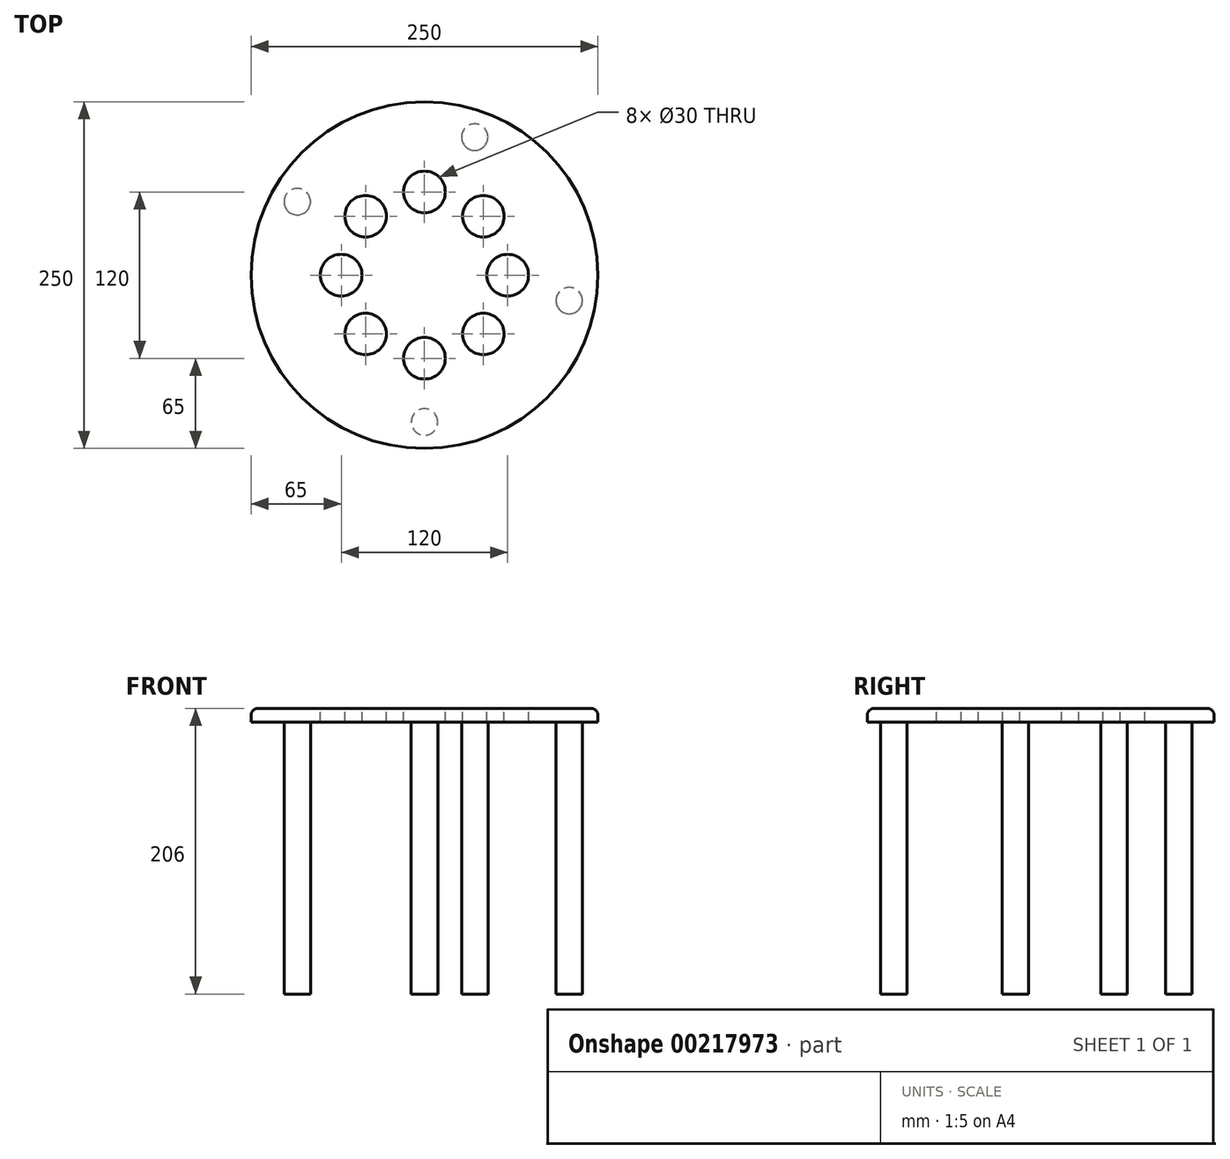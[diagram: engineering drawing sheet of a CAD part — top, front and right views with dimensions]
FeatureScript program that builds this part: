
annotation { "Feature Type Name" : "Feature", "Feature Type Description" : "" }
export const myFeature = defineFeature(function(context is Context, id is Id, definition is map)
    precondition{}
    {
        {
            var Q0;
            Q0=qCreatedBy(makeId("Top.planeOp"),FACE);
            var sketch = newSketch(context, id + "F0", { "sketchPlane" : qUnion([Q0])});
            skCircle(sketch, "E0", {"center": v(0, 0) * mm, "radius": 125 * mm});
            skSolve(sketch);
        }
        {
            var Q0;
            Q0=makeQuery(id+"F0.imprint","IMPRINT",FACE,{"disambiguationData":[TD([[makeQuery(id+"F0.imprint","IMPRINT",EDGE,{"derivedFrom":sQuery(id+"F0.wireOp",EDGE,"E0")}),1.0]])]});
            var sketch = newSketch(context, id + "F1", { "sketchPlane" : qUnion([Q0])});
            skCircle(sketch, "E1", {"center": v(0, 60) * mm, "radius": 15 * mm});
            skCircle(sketch, "E2.1.0", {"center": v(-42.43, 42.43) * mm, "radius": 15 * mm});
            skCircle(sketch, "E2.2.0", {"center": v(-60, 0) * mm, "radius": 15 * mm});
            skCircle(sketch, "E2.3.0", {"center": v(-42.43, -42.43) * mm, "radius": 15 * mm});
            skCircle(sketch, "E2.4.0", {"center": v(0, -60) * mm, "radius": 15 * mm});
            skCircle(sketch, "E2.5.0", {"center": v(42.43, -42.43) * mm, "radius": 15 * mm});
            skCircle(sketch, "E2.6.0", {"center": v(60, 0) * mm, "radius": 15 * mm});
            skCircle(sketch, "E2.7.0", {"center": v(42.43, 42.43) * mm, "radius": 15 * mm});
            skPoint(sketch, "E2.center", {"position": v(0, 0) * mm});
            skSolve(sketch);
        }
        {
            var Q0;
            Q0=makeQuery(id+"F0.imprint","IMPRINT",FACE,{"disambiguationData":[TD([[makeQuery(id+"F0.imprint","IMPRINT",EDGE,{"derivedFrom":sQuery(id+"F0.wireOp",EDGE,"E0")}),1.0]])]});
            extrude(context, id + "F2", {"entities" : qUnion([Q0]), "oppositeDirection" : true, "depth" : 10 * mm});
        }
        {
            var Q0;
            Q0=makeQuery(id+"F1.imprint","IMPRINT",FACE,{"disambiguationData":[TD([[makeQuery(id+"F1.imprint","IMPRINT",EDGE,{"derivedFrom":sQuery(id+"F1.wireOp",EDGE,"E2.1.0")}),1.0]])]});
            var Q1;
            Q1=makeQuery(id+"F1.imprint","IMPRINT",FACE,{"disambiguationData":[TD([[makeQuery(id+"F1.imprint","IMPRINT",EDGE,{"derivedFrom":sQuery(id+"F1.wireOp",EDGE,"E1")}),1.0]])]});
            var Q2;
            Q2=makeQuery(id+"F1.imprint","IMPRINT",FACE,{"disambiguationData":[TD([[makeQuery(id+"F1.imprint","IMPRINT",EDGE,{"derivedFrom":sQuery(id+"F1.wireOp",EDGE,"E2.7.0")}),1.0]])]});
            var Q3;
            Q3=makeQuery(id+"F1.imprint","IMPRINT",FACE,{"disambiguationData":[TD([[makeQuery(id+"F1.imprint","IMPRINT",EDGE,{"derivedFrom":sQuery(id+"F1.wireOp",EDGE,"E2.6.0")}),1.0]])]});
            var Q4;
            Q4=makeQuery(id+"F1.imprint","IMPRINT",FACE,{"disambiguationData":[TD([[makeQuery(id+"F1.imprint","IMPRINT",EDGE,{"derivedFrom":sQuery(id+"F1.wireOp",EDGE,"E2.5.0")}),1.0]])]});
            var Q5;
            Q5=makeQuery(id+"F1.imprint","IMPRINT",FACE,{"disambiguationData":[TD([[makeQuery(id+"F1.imprint","IMPRINT",EDGE,{"derivedFrom":sQuery(id+"F1.wireOp",EDGE,"E2.4.0")}),1.0]])]});
            var Q6;
            Q6=makeQuery(id+"F1.imprint","IMPRINT",FACE,{"disambiguationData":[TD([[makeQuery(id+"F1.imprint","IMPRINT",EDGE,{"derivedFrom":sQuery(id+"F1.wireOp",EDGE,"E2.3.0")}),1.0]])]});
            var Q7;
            Q7=makeQuery(id+"F1.imprint","IMPRINT",FACE,{"disambiguationData":[TD([[makeQuery(id+"F1.imprint","IMPRINT",EDGE,{"derivedFrom":sQuery(id+"F1.wireOp",EDGE,"E2.2.0")}),1.0]])]});
            extrude(context, id + "F3", {"entities" : qUnion([Q0, Q1, Q2, Q3, Q4, Q5, Q6, Q7]), "operationType" : NewBodyOperationType.REMOVE, "oppositeDirection" : true, "depth" : 10 * mm});
        }
        {
            var Q0;
            Q0=makeQuery(id+"F2.opExtrude","CAP_EDGE",EDGE,{"disambiguationData":[OSD([sQuery(id+"F0.wireOp",EDGE,"E0")])],"isStart":true});
            fillet(context, id + "F4", {"entities" : qUnion([Q0]), "radius" : 5 * mm, "tangentPropagation" : true, "allowEdgeOverflow" : false});
        }
        {
            var Q0;
            Q0=makeQuery(id+"F2.opExtrude","CAP_FACE",FACE,{"disambiguationData":[OSD([sQuery(id+"F0.wireOp",EDGE,"E0")])],"isStart":false});
            var sketch = newSketch(context, id + "F5", { "sketchPlane" : qUnion([Q0])});
            skCircle(sketch, "E3", {"center": v(0, 105.9) * mm, "radius": 9.54 * mm});
            skCircle(sketch, "E4.1.0", {"center": v(104.3, 18.4) * mm, "radius": 9.54 * mm});
            skCircle(sketch, "E4.2.0", {"center": v(36.22, -99.52) * mm, "radius": 9.54 * mm});
            skCircle(sketch, "E4.3.0", {"center": v(-91.72, -52.95) * mm, "radius": 9.54 * mm});
            skPoint(sketch, "E4.center", {"position": v(0, 0) * mm});
            skLineSegment(sketch, "E4.anchor1", {"start": v(0, 0) * mm, "end": v(0, 105.9) * mm, "construction": true});
            skLineSegment(sketch, "E4.anchor2", {"start": v(0, 0) * mm, "end": v(-91.72, -52.95) * mm, "construction": true});
            skSolve(sketch);
        }
        {
            var Q0;
            Q0=makeQuery(id+"F5.imprint","IMPRINT",FACE,{"disambiguationData":[TD([[makeQuery(id+"F5.imprint","IMPRINT",EDGE,{"derivedFrom":sQuery(id+"F5.wireOp",EDGE,"E3")}),1.0]])]});
            var Q1;
            Q1=makeQuery(id+"F5.imprint","IMPRINT",FACE,{"disambiguationData":[TD([[makeQuery(id+"F5.imprint","IMPRINT",EDGE,{"derivedFrom":sQuery(id+"F5.wireOp",EDGE,"E4.1.0")}),1.0]])]});
            var Q2;
            Q2=makeQuery(id+"F5.imprint","IMPRINT",FACE,{"disambiguationData":[TD([[makeQuery(id+"F5.imprint","IMPRINT",EDGE,{"derivedFrom":sQuery(id+"F5.wireOp",EDGE,"E4.2.0")}),1.0]])]});
            var Q3;
            Q3=makeQuery(id+"F5.imprint","IMPRINT",FACE,{"disambiguationData":[TD([[makeQuery(id+"F5.imprint","IMPRINT",EDGE,{"derivedFrom":sQuery(id+"F5.wireOp",EDGE,"E4.3.0")}),1.0]])]});
            extrude(context, id + "F6", {"entities" : qUnion([Q0, Q1, Q2, Q3]), "operationType" : NewBodyOperationType.ADD, "depth" : 196 * mm});
        }
    });
